FCSTD DOCUMENT  (FreeCAD 0.20R0.20)
Label: 015
License: All rights reserved
LicenseURL: http://en.wikipedia.org/wiki/All_rights_reserved
objects: Sketcher::SketchObject×2
note: 2 computed .brp shape members not serialized (recipe doc carries the construction recipe); baked Part::Feature solids carry a one-line shape summary decoded from their .brp

FEATURE [Sketcher::SketchObject] Sketch001  label="baseL"
  FullyConstrained = true
  sketch-geometry (26):
    g0: LineSegment StartX=0 StartY=0 StartZ=0 EndX=0 EndY=200 EndZ=0
    g1: LineSegment StartX=0 StartY=200 StartZ=0 EndX=190 EndY=200 EndZ=0
    g2: LineSegment StartX=0 StartY=0 StartZ=0 EndX=190 EndY=0 EndZ=0
    g3: LineSegment StartX=24 StartY=186 StartZ=0 EndX=172.826 EndY=114.213 EndZ=0
    g4: LineSegment StartX=16 StartY=178 StartZ=0 EndX=168.186 EndY=104.593 EndZ=0
    g5: LineSegment StartX=16 StartY=22 StartZ=0 EndX=168.186 EndY=95.4072 EndZ=0
    g6: LineSegment StartX=24 StartY=14 StartZ=0 EndX=172.826 EndY=85.7867 EndZ=0
    g7: LineSegment StartX=16 StartY=22 StartZ=0 EndX=16 EndY=178 EndZ=0
    g8: LineSegment StartX=200 StartY=94.0706 StartZ=0 EndX=209.626 EndY=89.4274 EndZ=0
    g9: LineSegment StartX=200 StartY=105.929 StartZ=0 EndX=209.626 EndY=110.573 EndZ=0
    g10: LineSegment StartX=24 StartY=14 StartZ=0 EndX=190 EndY=14 EndZ=0
    g11: LineSegment StartX=190 StartY=186 StartZ=0 EndX=24 EndY=186 EndZ=0
    g12: ArcOfCircle CenterX=190 CenterY=100 CenterZ=0 NormalX=0 NormalY=0 NormalZ=1 AngleXU=0 Radius=22.2927 StartAngle=0.494127 EndAngle=2.45024
    g13: ArcOfCircle CenterX=190 CenterY=100 CenterZ=0 NormalX=0 NormalY=0 NormalZ=1 AngleXU=0 Radius=11.6257 StartAngle=0.535213 EndAngle=5.74797
    g14: LineSegment StartX=190 StartY=200 StartZ=0 EndX=190 EndY=195.3 EndZ=0
    g15: LineSegment StartX=190 StartY=195.3 StartZ=0 EndX=186.638 EndY=195.3 EndZ=0
    g16: ArcOfCircle CenterX=184 CenterY=193 CenterZ=0 NormalX=0 NormalY=0 NormalZ=1 AngleXU=0 Radius=3.5 StartAngle=0.717022 EndAngle=5.56616
    g17: LineSegment StartX=190 StartY=186 StartZ=0 EndX=190 EndY=190.7 EndZ=0
    g18: LineSegment StartX=190 StartY=190.7 StartZ=0 EndX=186.638 EndY=190.7 EndZ=0
    g19: LineSegment StartX=190 StartY=14 StartZ=0 EndX=190 EndY=9 EndZ=0
    g20: LineSegment StartX=190 StartY=9 StartZ=0 EndX=193.652 EndY=9 EndZ=0
    g21: LineSegment StartX=190 StartY=0 StartZ=0 EndX=190 EndY=5 EndZ=0
    g22: ArcOfCircle CenterX=196.15 CenterY=7 CenterZ=0 NormalX=0 NormalY=0 NormalZ=1 AngleXU=0 Radius=3.2 StartAngle=3.81672 EndAngle=8.74965
    g23: LineSegment StartX=190 StartY=5 StartZ=0 EndX=193.652 EndY=5 EndZ=0
    g24: ArcOfCircle CenterX=190 CenterY=100 CenterZ=0 NormalX=0 NormalY=0 NormalZ=1 AngleXU=0 Radius=22.2927 StartAngle=3.83294 EndAngle=5.78906
    g25: ArcOfCircle CenterX=190 CenterY=100 CenterZ=0 NormalX=0 NormalY=0 NormalZ=1 AngleXU=0 Radius=22.2927 StartAngle=2.93408 EndAngle=3.3491
  constraints (67):
    c: Coincident(g0,g-1)
    c: Vertical(g0)
    c: Distance(g0) = 200
    c: Coincident(g1,g0)
    c: Horizontal(g1)
    c: Distance(g1) = 190
    c: Coincident(g2,g0)
    c: Horizontal(g2)
    c: Distance(g2) = 190
    c: Block(g3)
    c: Block(g4)
    c: Block(g6)
    c: Block(g5)
    c: Vertical(g7)
    c: Block(g7)
    c: Block(g9)
    c: Block(g8)
    c: Coincident(g10,g6)
    c: Horizontal(g10)
    c: Coincident(g11,g3)
    c: Horizontal(g11)
    c: Block(g11)
    c: Coincident(g14,g1)
    c: Vertical(g14)
    c: Distance(g14) = 4.7
    c: Coincident(g15,g14)
    c: Horizontal(g15)
    c: Coincident(g17,g11)
    c: Vertical(g17)
    c: Distance(g17) = 4.7
    c: Coincident(g18,g17)
    c: Block(g18)
    c: Block(g10)
    c: Coincident(g19,g10)
    c: Vertical(g19)
    c: Distance(g19) = 5
    c: Coincident(g20,g19)
    c: Horizontal(g20)
    c: Coincident(g21,g2)
    c: Vertical(g21)
    c: Distance(g21) = 5
    c: Coincident(g23,g21)
    c: Horizontal(g23)
    c: Block(g23)
    c: Block(g22)
    c: Coincident(g22,g20)
    c: Coincident(g22,g23)
    c: Block(g20)
    c: Block(g19)
    c: Block(g16)
    c: Coincident(g16,g18)
    c: Coincident(g16,g15)
    c: Block(g15)
    c: Coincident(g13,g8)
    c: Coincident(g13,g9)
    c: Block(g13)
    c: Block(g12)
    c: Coincident(g9,g12)
    c: Coincident(g8,g24)
    c: Equal(g12,g24)
    c: Coincident(g25,g5)
    c: Coincident(g24,g6)
    c: Coincident(g12,g24)
    c: Equal(g12,g25)
    c: Coincident(g12,g3)
    c: Coincident(g25,g4)
    c: Coincident(g12,g25)
FEATURE [Sketcher::SketchObject] Sketch002  label="baseR"
  FullyConstrained = true
  sketch-geometry (25):
    g0: LineSegment StartX=390 StartY=200 StartZ=0 EndX=390 EndY=0 EndZ=0
    g1: LineSegment StartX=390 StartY=200 StartZ=0 EndX=200 EndY=200 EndZ=0
    g2: LineSegment StartX=390 StartY=0 StartZ=0 EndX=200 EndY=0 EndZ=0
    g3: LineSegment StartX=212.293 StartY=100 StartZ=0 EndX=374 EndY=22 EndZ=0
    g4: LineSegment StartX=217.615 StartY=85.5738 StartZ=0 EndX=366 EndY=14 EndZ=0
    g5: LineSegment StartX=374 StartY=178 StartZ=0 EndX=212.293 EndY=100 EndZ=0
    g6: LineSegment StartX=217.615 StartY=114.426 StartZ=0 EndX=366 EndY=186 EndZ=0
    g7: LineSegment StartX=374 StartY=178 StartZ=0 EndX=374 EndY=22 EndZ=0
    g8: LineSegment StartX=366 StartY=14 StartZ=0 EndX=200 EndY=14 EndZ=0
    g9: LineSegment StartX=200 StartY=186 StartZ=0 EndX=366 EndY=186 EndZ=0
    g10: ArcOfCircle CenterX=200 CenterY=100 CenterZ=0 NormalX=0 NormalY=0 NormalZ=1 AngleXU=0 Radius=11.2273 StartAngle=0.945168 EndAngle=5.33802
    g11: LineSegment StartX=200 StartY=200 StartZ=0 EndX=200 EndY=195 EndZ=0
    g12: LineSegment StartX=200 StartY=186 StartZ=0 EndX=200 EndY=191 EndZ=0
    g13: LineSegment StartX=200 StartY=191 StartZ=0 EndX=196.348 EndY=191 EndZ=0
    g14: ArcOfCircle CenterX=193.85 CenterY=193 CenterZ=0 NormalX=0 NormalY=0 NormalZ=1 AngleXU=0 Radius=3.2 StartAngle=0.675132 EndAngle=5.60805
    g15: LineSegment StartX=200 StartY=195 StartZ=0 EndX=196.348 EndY=195 EndZ=0
    g16: LineSegment StartX=200 StartY=14 StartZ=0 EndX=200 EndY=9.3 EndZ=0
    g17: LineSegment StartX=200 StartY=9.3 StartZ=0 EndX=203.362 EndY=9.3 EndZ=0
    g18: ArcOfCircle CenterX=206 CenterY=7 CenterZ=0 NormalX=0 NormalY=0 NormalZ=1 AngleXU=0 Radius=3.5 StartAngle=3.85861 EndAngle=8.70776
    g19: LineSegment StartX=200 StartY=0 StartZ=0 EndX=200 EndY=4.7 EndZ=0
    g20: LineSegment StartX=200 StartY=4.7 StartZ=0 EndX=203.362 EndY=4.7 EndZ=0
    g21: LineSegment StartX=206.575 StartY=109.101 StartZ=0 EndX=206.575 EndY=108.801 EndZ=0
    g22: LineSegment StartX=206.575 StartY=90.8992 StartZ=0 EndX=206.575 EndY=91.1992 EndZ=0
    g23: LineSegment StartX=206.575 StartY=108.801 StartZ=0 EndX=217.615 EndY=114.426 EndZ=0
    g24: LineSegment StartX=206.575 StartY=91.1992 StartZ=0 EndX=217.615 EndY=85.5738 EndZ=0
  constraints (59):
    c: Vertical(g0)
    c: Block(g0)
    c: Coincident(g1,g0)
    c: Horizontal(g1)
    c: Coincident(g2,g0)
    c: Horizontal(g2)
    c: Distance(g2) = 190
    c: Distance(g1) = 190
    c: Block(g6)
    c: Block(g5)
    c: Block(g3)
    c: Block(g4)
    c: Coincident(g3,g5)
    c: Coincident(g7,g5)
    c: Coincident(g7,g3)
    c: Vertical(g7)
    c: Coincident(g8,g4)
    c: Coincident(g9,g6)
    c: Coincident(g11,g1)
    c: Vertical(g11)
    c: Block(g9)
    c: Coincident(g12,g9)
    c: Vertical(g12)
    c: Distance(g12) = 5
    c: Coincident(g13,g12)
    c: Horizontal(g13)
    c: Coincident(g15,g11)
    c: Block(g15)
    c: Block(g8)
    c: Coincident(g16,g8)
    c: Vertical(g16)
    c: Distance(g16) = 4.7
    c: Coincident(g17,g16)
    c: Horizontal(g17)
    c: Coincident(g19,g2)
    c: Vertical(g19)
    c: Coincident(g20,g19)
    c: Block(g20)
    c: Block(g18)
    c: Coincident(g18,g17)
    c: Coincident(g18,g20)
    c: Block(g14)
    c: Coincident(g14,g13)
    c: Coincident(g14,g15)
    c: Block(g10)
    c: Coincident(g21,g10)
    c: Vertical(g21)
    c: Coincident(g22,g10)
    c: Vertical(g22)
    c: Distance(g21) = 0.3
    c: Distance(g22) = 0.3
    c: Coincident(g23,g21)
    c: Angle(g23,g21) = 1.09956
    c: Coincident(g24,g22)
    c: Angle(g22,g24) = 1.09956
    c: Block(g24)
    c: Block(g23)
    c: Coincident(g4,g24)
    c: Coincident(g6,g23)
